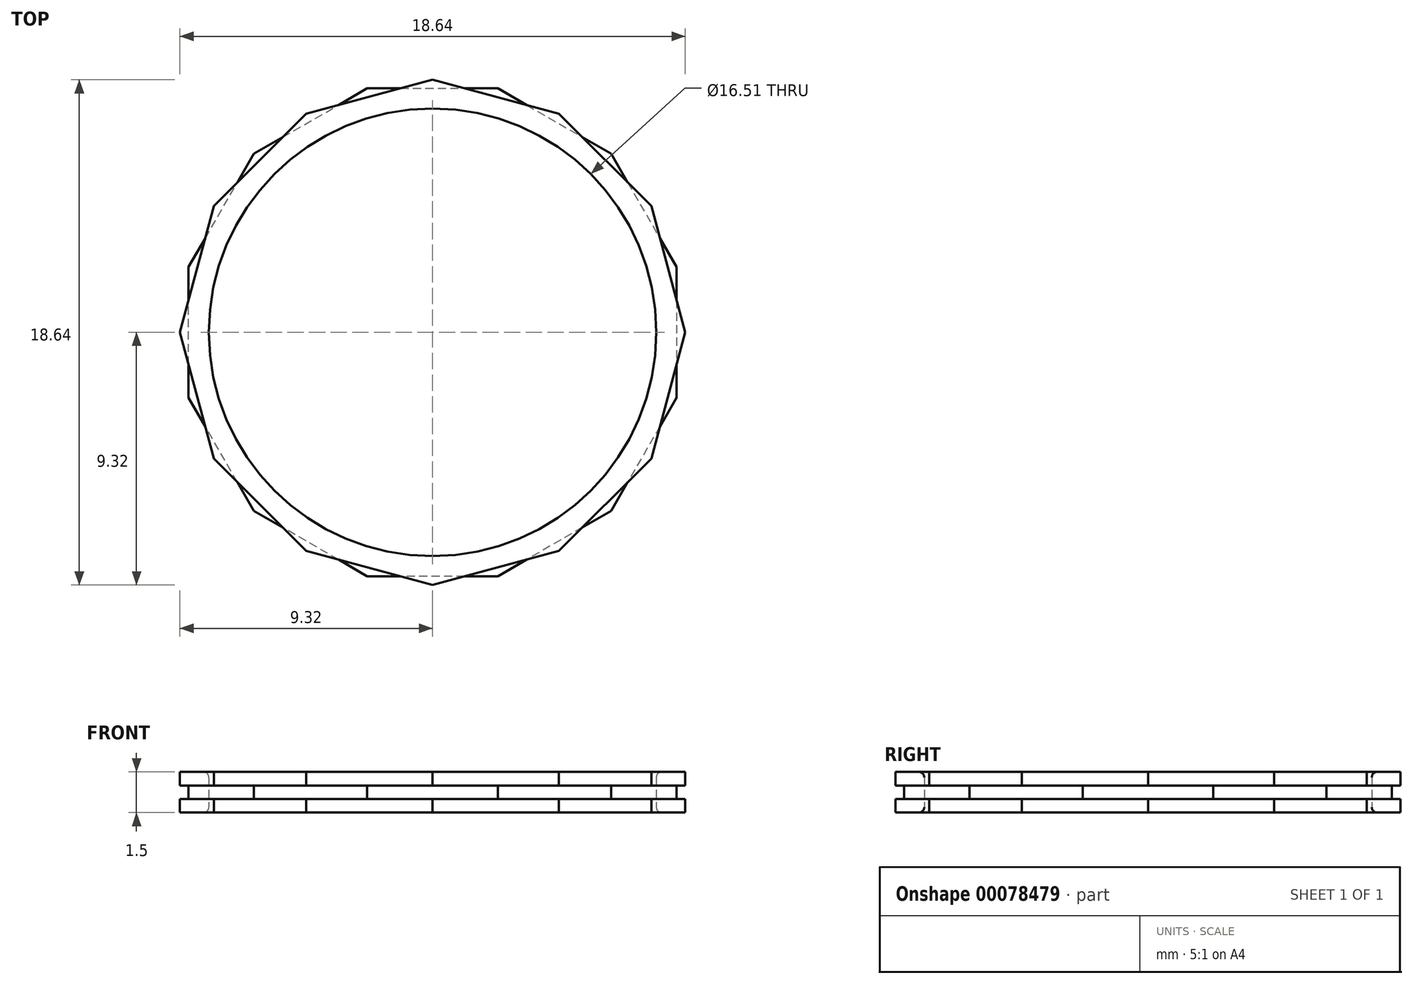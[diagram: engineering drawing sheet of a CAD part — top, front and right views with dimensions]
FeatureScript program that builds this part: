
annotation { "Feature Type Name" : "Feature", "Feature Type Description" : "" }
export const myFeature = defineFeature(function(context is Context, id is Id, definition is map)
    precondition{}
    {
        {
            var Q0;
            Q0=qCreatedBy(makeId("Top.planeOp"),FACE);
            var sketch = newSketch(context, id + "F0", { "sketchPlane" : qUnion([Q0])});
            skCircle(sketch, "E0", {"center": v(0, 0) * mm, "radius": 8.26 * mm});
            skSolve(sketch);
        }
        {
            var Q0;
            Q0=qCreatedBy(makeId("Top.planeOp"),FACE);
            var sketch = newSketch(context, id + "F1", { "sketchPlane" : qUnion([Q0])});
            skCircle(sketch, "E1.cCircle", {"center": v(0, 0) * mm, "radius": 9 * mm, "construction": true});
            skLineSegment(sketch, "E1.0", {"start": v(-6.59, -6.59) * mm, "end": v(-9, -2.41) * mm});
            skLineSegment(sketch, "E1.1", {"start": v(-9, -2.41) * mm, "end": v(-9, 2.41) * mm});
            skLineSegment(sketch, "E1.2", {"start": v(-9, 2.41) * mm, "end": v(-6.59, 6.59) * mm});
            skLineSegment(sketch, "E1.3", {"start": v(-6.59, 6.59) * mm, "end": v(-2.41, 9) * mm});
            skLineSegment(sketch, "E1.4", {"start": v(-2.41, 9) * mm, "end": v(2.41, 9) * mm});
            skLineSegment(sketch, "E1.5", {"start": v(2.41, 9) * mm, "end": v(6.59, 6.59) * mm});
            skLineSegment(sketch, "E1.6", {"start": v(6.59, 6.59) * mm, "end": v(9, 2.41) * mm});
            skLineSegment(sketch, "E1.7", {"start": v(9, 2.41) * mm, "end": v(9, -2.41) * mm});
            skLineSegment(sketch, "E1.8", {"start": v(9, -2.41) * mm, "end": v(6.59, -6.59) * mm});
            skLineSegment(sketch, "E1.9", {"start": v(6.59, -6.59) * mm, "end": v(2.41, -9) * mm});
            skLineSegment(sketch, "E1.10", {"start": v(2.41, -9) * mm, "end": v(-2.41, -9) * mm});
            skLineSegment(sketch, "E1.11", {"start": v(-2.41, -9) * mm, "end": v(-6.59, -6.59) * mm});
            skPoint(sketch, "E1.0.midPoint", {"position": v(-7.8, -4.5) * mm});
            skLineSegment(sketch, "E2", {"start": v(0, 0) * mm, "end": v(-9, 0) * mm, "construction": true});
            skSolve(sketch);
        }
        {
            var Q0;
            Q0 = qSketchRegion(id + "F1", true);
            extrude(context, id + "F2", {"entities" : qUnion([Q0]), "endBound" : BoundingType.SYMMETRIC, "depth" : .5 * mm});
        }
        {
            var Q0;
            Q0=makeQuery(id+"F2.opExtrude","CAP_FACE",FACE,{"disambiguationData":[OSD([sQuery(id+"F1.wireOp",EDGE,"E1.0"),sQuery(id+"F1.wireOp",EDGE,"E1.1"),sQuery(id+"F1.wireOp",EDGE,"E1.2"),sQuery(id+"F1.wireOp",EDGE,"E1.3"),sQuery(id+"F1.wireOp",EDGE,"E1.4"),sQuery(id+"F1.wireOp",EDGE,"E1.5"),sQuery(id+"F1.wireOp",EDGE,"E1.6"),sQuery(id+"F1.wireOp",EDGE,"E1.7"),sQuery(id+"F1.wireOp",EDGE,"E1.8"),sQuery(id+"F1.wireOp",EDGE,"E1.9"),sQuery(id+"F1.wireOp",EDGE,"E1.10"),sQuery(id+"F1.wireOp",EDGE,"E1.11")])],"isStart":false});
            var sketch = newSketch(context, id + "F3", { "sketchPlane" : qUnion([Q0])});
            skCircle(sketch, "E3.cCircle", {"center": v(0, 0) * mm, "radius": 9 * mm, "construction": true});
            skLineSegment(sketch, "E3.0", {"start": v(-9.32, 0) * mm, "end": v(-8.07, 4.66) * mm});
            skLineSegment(sketch, "E3.1", {"start": v(-8.07, 4.66) * mm, "end": v(-4.66, 8.07) * mm});
            skLineSegment(sketch, "E3.2", {"start": v(-4.66, 8.07) * mm, "end": v(0, 9.32) * mm});
            skLineSegment(sketch, "E3.3", {"start": v(0, 9.32) * mm, "end": v(4.66, 8.07) * mm});
            skLineSegment(sketch, "E3.4", {"start": v(4.66, 8.07) * mm, "end": v(8.07, 4.66) * mm});
            skLineSegment(sketch, "E3.5", {"start": v(8.07, 4.66) * mm, "end": v(9.32, 0) * mm});
            skLineSegment(sketch, "E3.6", {"start": v(9.32, 0) * mm, "end": v(8.07, -4.66) * mm});
            skLineSegment(sketch, "E3.7", {"start": v(8.07, -4.66) * mm, "end": v(4.66, -8.07) * mm});
            skLineSegment(sketch, "E3.8", {"start": v(4.66, -8.07) * mm, "end": v(0, -9.32) * mm});
            skLineSegment(sketch, "E3.9", {"start": v(0, -9.32) * mm, "end": v(-4.66, -8.07) * mm});
            skLineSegment(sketch, "E3.10", {"start": v(-4.66, -8.07) * mm, "end": v(-8.07, -4.66) * mm});
            skLineSegment(sketch, "E3.11", {"start": v(-8.07, -4.66) * mm, "end": v(-9.32, 0) * mm});
            skPoint(sketch, "E3.0.midPoint", {"position": v(-8.7, 2.33) * mm});
            skLineSegment(sketch, "E4", {"start": v(0, 0) * mm, "end": v(-8.7, 2.33) * mm, "construction": true});
            skSolve(sketch);
        }
        {
            var Q0;
            Q0 = qSketchRegion(id + "F3", true);
            extrude(context, id + "F4", {"entities" : qUnion([Q0]), "depth" : .5 * mm});
        }
        {
            var Q0;
            Q0=makeQuery(id+"F4.opExtrude","SWEPT_BODY",BODY,{"disambiguationData":[OSD([sQuery(id+"F3.wireOp",EDGE,"E3.0"),sQuery(id+"F3.wireOp",EDGE,"E3.1"),sQuery(id+"F3.wireOp",EDGE,"E3.2"),sQuery(id+"F3.wireOp",EDGE,"E3.3"),sQuery(id+"F3.wireOp",EDGE,"E3.4"),sQuery(id+"F3.wireOp",EDGE,"E3.5"),sQuery(id+"F3.wireOp",EDGE,"E3.6"),sQuery(id+"F3.wireOp",EDGE,"E3.7"),sQuery(id+"F3.wireOp",EDGE,"E3.8"),sQuery(id+"F3.wireOp",EDGE,"E3.9"),sQuery(id+"F3.wireOp",EDGE,"E3.10"),sQuery(id+"F3.wireOp",EDGE,"E3.11")])]});
            var Q1;
            Q1=qCreatedBy(makeId("Top.planeOp"),FACE);
            mirror(context, id + "F5", {"operationType" : NewBodyOperationType.ADD, "entities" : qUnion([Q0]), "mirrorPlane" : qUnion([Q1])});
        }
        {
            var Q0;
            Q0 = qSketchRegion(id + "F0", true);
            extrude(context, id + "F6", {"entities" : qUnion([Q0]), "operationType" : NewBodyOperationType.REMOVE, "endBound" : BoundingType.SYMMETRIC, "depth" : 5 * mm});
        }
        {
            var Q0;
            Q0=makeQuery(id+"F6.boolean.opBoolean","COPY",FACE,{"derivedFrom":makeQuery(id+"F6.opExtrude","SWEPT_FACE",FACE,{"disambiguationData":[OSD([sQuery(id+"F0.wireOp",EDGE,"E0")])]})});
            fillet(context, id + "F7", {"entities" : qUnion([Q0]), "radius" : .2 * mm, "tangentPropagation" : true, "allowEdgeOverflow" : false});
        }
    });
